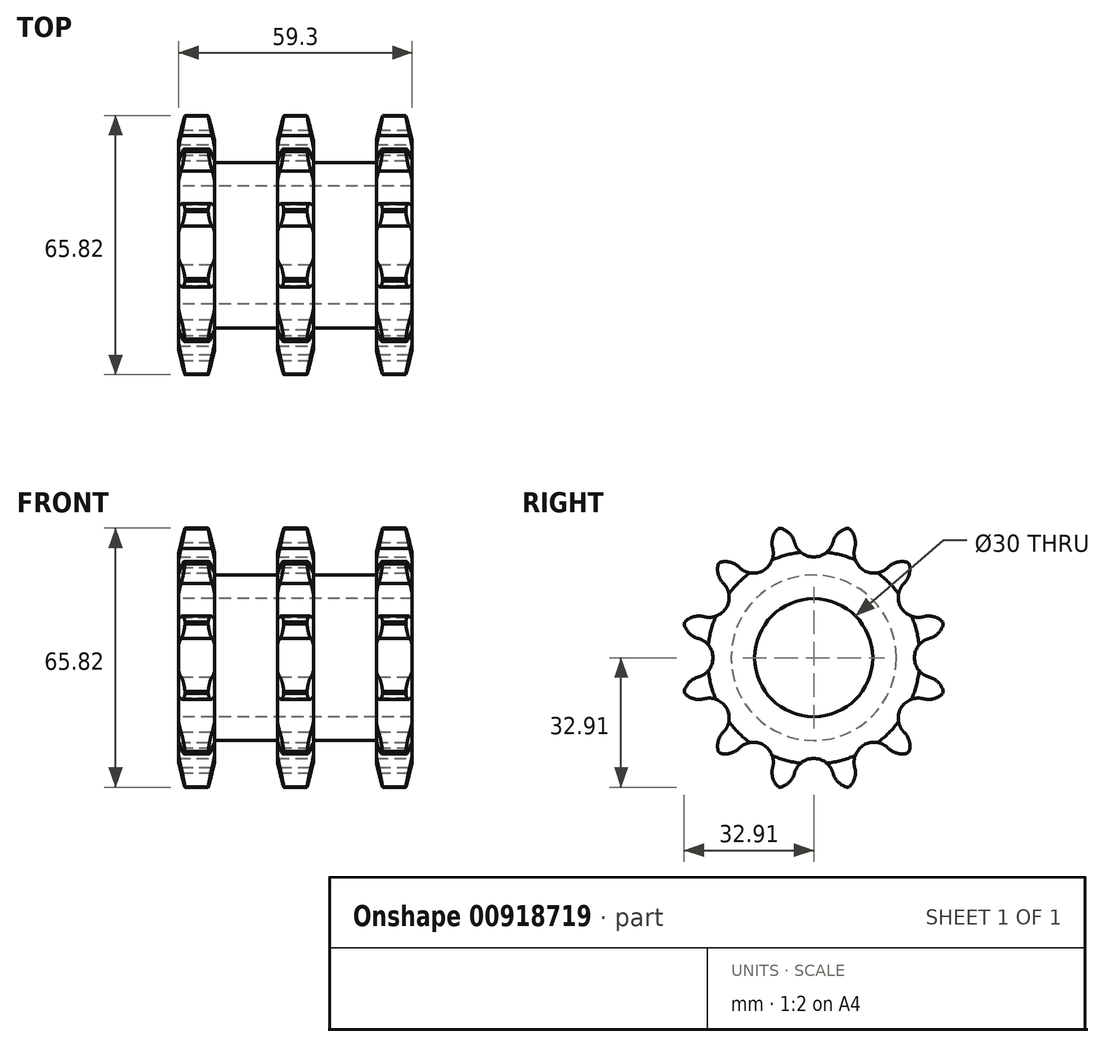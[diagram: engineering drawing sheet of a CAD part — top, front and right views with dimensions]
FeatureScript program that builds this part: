
annotation { "Feature Type Name" : "Feature", "Feature Type Description" : "" }
export const myFeature = defineFeature(function(context is Context, id is Id, definition is map)
    precondition{}
    {
        {
            var Q0;
            Q0=qCreatedBy(makeId("Front.planeOp"),FACE);
            var sketch = newSketch(context, id + "F0", { "sketchPlane" : qUnion([Q0])});
            skLineSegment(sketch, "E0", {"start": v(-60.79, 0) * mm, "end": v(61.07, 0) * mm, "construction": true});
            skLineSegment(sketch, "E1.bottom", {"start": v(-59.3, 34) * mm, "end": v(-50.2, 34) * mm});
            skLineSegment(sketch, "E1.top", {"start": v(-59.3, 15) * mm, "end": v(0, 15) * mm});
            skLineSegment(sketch, "E1.left", {"start": v(-59.3, 34) * mm, "end": v(-59.3, 15) * mm});
            skLineSegment(sketch, "E1.right", {"start": v(-50.2, 34) * mm, "end": v(-50.2, 21) * mm});
            skLineSegment(sketch, "E2.bottom", {"start": v(-50.2, 21) * mm, "end": v(-34.2, 21) * mm});
            skLineSegment(sketch, "E2.top", {"start": v(-59.3, 15) * mm, "end": v(-34.2, 15) * mm});
            skLineSegment(sketch, "E2.left", {"start": v(-59.3, 21) * mm, "end": v(-59.3, 15) * mm});
            skLineSegment(sketch, "E3.bottom", {"start": v(-34.2, 34) * mm, "end": v(-25.1, 34) * mm});
            skLineSegment(sketch, "E3.top", {"start": v(-34.2, 15) * mm, "end": v(-25.1, 15) * mm});
            skLineSegment(sketch, "E3.left", {"start": v(-34.2, 34) * mm, "end": v(-34.2, 21) * mm});
            skLineSegment(sketch, "E3.right", {"start": v(-25.1, 34) * mm, "end": v(-25.1, 21) * mm});
            skLineSegment(sketch, "E4.bottom", {"start": v(-25.1, 21) * mm, "end": v(-9.1, 21) * mm});
            skLineSegment(sketch, "E4.top", {"start": v(0, 15) * mm, "end": v(0, 15) * mm});
            skLineSegment(sketch, "E5", {"start": v(0, 15) * mm, "end": v(0, -11) * mm, "construction": true});
            skLineSegment(sketch, "E6.bottom", {"start": v(-9.1, 15) * mm, "end": v(0, 15) * mm});
            skLineSegment(sketch, "E6.top", {"start": v(-9.1, 34) * mm, "end": v(0, 34) * mm});
            skLineSegment(sketch, "E6.left", {"start": v(0, 15) * mm, "end": v(0, 34) * mm});
            skLineSegment(sketch, "E6.right", {"start": v(-9.1, 21) * mm, "end": v(-9.1, 34) * mm});
            skPoint(sketch, "E7.orphan", {"position": v(-50.2, 15) * mm});
            skPoint(sketch, "E8.orphan", {"position": v(0, 43.23) * mm});
            skSolve(sketch);
        }
        {
            var Q0;
            Q0=makeQuery(id+"F0.imprint","IMPRINT",FACE,{"disambiguationData":[TD([[makeQuery(id+"F0.imprint","IMPRINT",EDGE,{"derivedFrom":sQuery(id+"F0.wireOp",EDGE,"E1.bottom")}),-1.0]])]});
            var Q1;
            Q1=sQuery(id+"F0.wireOp",EDGE,"E0");
            revolve(context, id + "F1", {"surfaceOperationType" : NewSurfaceOperationType.NEW, "entities" : qUnion([Q0]), "axis" : qUnion([Q1]), "revolveType" : RevolveType.FULL});
        }
        {
            var Q0;
            Q0=makeQuery(id+"F1.opRevolve","SWEPT_FACE",FACE,{"disambiguationData":[OSD([sQuery(id+"F0.wireOp",EDGE,"E6.left")])]});
            var sketch = newSketch(context, id + "F2", { "sketchPlane" : qUnion([Q0])});
            skArc(sketch, "E9", {"start": v(-23.84, 24.24) * mm, "mid": v(-24.04, 24.04) * mm, "end": v(-24.24, 23.84) * mm});
            skCircle(sketch, "E10", {"center": v(0, 0) * mm, "radius": 30.67 * mm, "construction": true});
            skCircle(sketch, "E11", {"center": v(0, 0) * mm, "radius": 29.7 * mm, "construction": true});
            skLineSegment(sketch, "E12", {"start": v(0, 0) * mm, "end": v(5.78, 30.12) * mm, "construction": true});
            skLineSegment(sketch, "E13", {"start": v(0, 0) * mm, "end": v(10.05, 28.98) * mm, "construction": true});
            skArc(sketch, "E14", {"start": v(8.53, 32.92) * mm, "mid": v(6.21, 31.61) * mm, "end": v(4.9, 29.3) * mm});
            skArc(sketch, "E15.1.0", {"start": v(-9.07, 32.77) * mm, "mid": v(-10.42, 30.48) * mm, "end": v(-10.41, 27.82) * mm});
            skArc(sketch, "E16.trimOffspring", {"start": v(10.41, 27.82) * mm, "mid": v(10.42, 30.48) * mm, "end": v(9.07, 32.77) * mm});
            skArc(sketch, "E17.trimOffspring", {"start": v(-4.9, 29.36) * mm, "mid": v(-0.03, 25.6) * mm, "end": v(4.9, 29.3) * mm});
            skArc(sketch, "E18.trimOffspring", {"start": v(-4.9, 29.3) * mm, "mid": v(-6.21, 31.61) * mm, "end": v(-8.53, 32.92) * mm});
            skArc(sketch, "E19.1.0", {"start": v(-18.93, 22.97) * mm, "mid": v(-12.82, 22.15) * mm, "end": v(-10.41, 27.82) * mm});
            skArc(sketch, "E19.2.0", {"start": v(-27.88, 10.43) * mm, "mid": v(-22.18, 12.77) * mm, "end": v(-22.93, 18.89) * mm});
            skArc(sketch, "E19.3.0", {"start": v(-29.36, -4.9) * mm, "mid": v(-25.6, -0.03) * mm, "end": v(-29.3, 4.9) * mm});
            skArc(sketch, "E19.4.0", {"start": v(-22.97, -18.92) * mm, "mid": v(-22.15, -12.82) * mm, "end": v(-27.82, -10.4) * mm});
            skArc(sketch, "E19.5.0", {"start": v(-10.43, -27.87) * mm, "mid": v(-12.77, -22.17) * mm, "end": v(-18.88, -22.92) * mm});
            skArc(sketch, "E19.6.0", {"start": v(4.9, -29.35) * mm, "mid": v(0.03, -25.59) * mm, "end": v(-4.9, -29.3) * mm});
            skArc(sketch, "E19.7.0", {"start": v(18.93, -22.97) * mm, "mid": v(12.82, -22.14) * mm, "end": v(10.41, -27.81) * mm});
            skArc(sketch, "E19.8.0", {"start": v(27.88, -10.42) * mm, "mid": v(22.18, -12.77) * mm, "end": v(22.93, -18.88) * mm});
            skArc(sketch, "E19.9.0", {"start": v(29.36, 4.91) * mm, "mid": v(25.6, 0.03) * mm, "end": v(29.3, -4.89) * mm});
            skArc(sketch, "E19.10.0", {"start": v(22.97, 18.93) * mm, "mid": v(22.15, 12.82) * mm, "end": v(27.82, 10.42) * mm});
            skArc(sketch, "E19.11.0", {"start": v(10.43, 27.88) * mm, "mid": v(12.77, 22.18) * mm, "end": v(18.88, 22.93) * mm});
            skArc(sketch, "E20.1.0", {"start": v(-9.07, 32.77) * mm, "mid": v(-10.43, 30.48) * mm, "end": v(-10.41, 27.82) * mm});
            skArc(sketch, "E20.2.0", {"start": v(-24.24, 23.84) * mm, "mid": v(-24.27, 21.18) * mm, "end": v(-22.93, 18.89) * mm});
            skArc(sketch, "E20.3.0", {"start": v(-32.91, 8.53) * mm, "mid": v(-31.6, 6.21) * mm, "end": v(-29.3, 4.9) * mm});
            skArc(sketch, "E20.4.0", {"start": v(-32.77, -9.07) * mm, "mid": v(-30.48, -10.42) * mm, "end": v(-27.82, -10.4) * mm});
            skArc(sketch, "E20.5.0", {"start": v(-23.84, -24.24) * mm, "mid": v(-21.18, -24.26) * mm, "end": v(-18.88, -22.92) * mm});
            skArc(sketch, "E20.6.0", {"start": v(-8.53, -32.9) * mm, "mid": v(-6.21, -31.6) * mm, "end": v(-4.9, -29.3) * mm});
            skArc(sketch, "E20.7.0", {"start": v(9.07, -32.76) * mm, "mid": v(10.43, -30.47) * mm, "end": v(10.41, -27.81) * mm});
            skArc(sketch, "E20.8.0", {"start": v(24.24, -23.84) * mm, "mid": v(24.27, -21.18) * mm, "end": v(22.93, -18.88) * mm});
            skArc(sketch, "E20.9.0", {"start": v(32.91, -8.52) * mm, "mid": v(31.6, -6.2) * mm, "end": v(29.3, -4.89) * mm});
            skArc(sketch, "E20.10.0", {"start": v(32.77, 9.07) * mm, "mid": v(30.48, 10.43) * mm, "end": v(27.82, 10.42) * mm});
            skArc(sketch, "E20.11.0", {"start": v(23.84, 24.24) * mm, "mid": v(21.18, 24.27) * mm, "end": v(18.88, 22.93) * mm});
            skArc(sketch, "E21.2.0", {"start": v(-18.88, 22.93) * mm, "mid": v(-21.18, 24.27) * mm, "end": v(-23.84, 24.24) * mm});
            skArc(sketch, "E21.3.0", {"start": v(-27.82, 10.42) * mm, "mid": v(-30.48, 10.43) * mm, "end": v(-32.77, 9.07) * mm});
            skArc(sketch, "E21.4.0", {"start": v(-29.3, -4.89) * mm, "mid": v(-31.6, -6.2) * mm, "end": v(-32.91, -8.52) * mm});
            skArc(sketch, "E21.5.0", {"start": v(-22.93, -18.88) * mm, "mid": v(-24.27, -21.18) * mm, "end": v(-24.24, -23.84) * mm});
            skArc(sketch, "E21.6.0", {"start": v(-10.41, -27.81) * mm, "mid": v(-10.42, -30.47) * mm, "end": v(-9.07, -32.76) * mm});
            skArc(sketch, "E21.7.0", {"start": v(4.9, -29.3) * mm, "mid": v(6.21, -31.6) * mm, "end": v(8.53, -32.9) * mm});
            skArc(sketch, "E21.8.0", {"start": v(18.88, -22.92) * mm, "mid": v(21.18, -24.26) * mm, "end": v(23.84, -24.24) * mm});
            skArc(sketch, "E21.9.0", {"start": v(27.82, -10.4) * mm, "mid": v(30.48, -10.42) * mm, "end": v(32.77, -9.07) * mm});
            skArc(sketch, "E21.10.0", {"start": v(29.3, 4.9) * mm, "mid": v(31.6, 6.21) * mm, "end": v(32.91, 8.53) * mm});
            skArc(sketch, "E21.11.0", {"start": v(22.93, 18.89) * mm, "mid": v(24.27, 21.19) * mm, "end": v(24.24, 23.85) * mm});
            skArc(sketch, "E22.trimOffspring", {"start": v(-32.77, 9.07) * mm, "mid": v(-32.84, 8.8) * mm, "end": v(-32.91, 8.53) * mm});
            skArc(sketch, "E23.trimOffspring", {"start": v(-32.91, -8.52) * mm, "mid": v(-32.84, -8.8) * mm, "end": v(-32.77, -9.07) * mm});
            skArc(sketch, "E24.trimOffspring", {"start": v(-24.24, -23.84) * mm, "mid": v(-24.04, -24.04) * mm, "end": v(-23.84, -24.24) * mm});
            skArc(sketch, "E25.trimOffspring", {"start": v(-9.07, -32.76) * mm, "mid": v(-8.8, -32.84) * mm, "end": v(-8.53, -32.9) * mm});
            skArc(sketch, "E26.trimOffspring", {"start": v(8.53, -32.9) * mm, "mid": v(8.8, -32.84) * mm, "end": v(9.07, -32.76) * mm});
            skArc(sketch, "E27.trimOffspring", {"start": v(23.84, -24.24) * mm, "mid": v(24.04, -24.04) * mm, "end": v(24.24, -23.84) * mm});
            skArc(sketch, "E28.trimOffspring", {"start": v(32.77, -9.07) * mm, "mid": v(32.84, -8.8) * mm, "end": v(32.91, -8.52) * mm});
            skArc(sketch, "E29.trimOffspring", {"start": v(32.91, 8.53) * mm, "mid": v(32.84, 8.8) * mm, "end": v(32.77, 9.07) * mm});
            skArc(sketch, "E30.trimOffspring", {"start": v(24.24, 23.85) * mm, "mid": v(24.04, 24.05) * mm, "end": v(23.84, 24.24) * mm});
            skArc(sketch, "E31.trimOffspring", {"start": v(9.07, 32.77) * mm, "mid": v(8.8, 32.84) * mm, "end": v(8.53, 32.92) * mm});
            skArc(sketch, "E32.trimOffspring", {"start": v(-8.53, 32.92) * mm, "mid": v(-8.8, 32.84) * mm, "end": v(-9.07, 32.77) * mm});
            skSolve(sketch);
        }
        {
            var Q0;
            Q0=makeQuery(id+"F1.opRevolve","SWEPT_EDGE",EDGE,{"disambiguationData":[OSD([sQuery(id+"F0.wireOp",EDGE,"E6.top"),sQuery(id+"F0.wireOp",EDGE,"E6.right")])]});
            var Q1;
            Q1=makeQuery(id+"F1.opRevolve","SWEPT_EDGE",EDGE,{"disambiguationData":[OSD([sQuery(id+"F0.wireOp",EDGE,"E3.bottom"),sQuery(id+"F0.wireOp",EDGE,"E3.left")])]});
            var Q2;
            Q2=makeQuery(id+"F1.opRevolve","SWEPT_EDGE",EDGE,{"disambiguationData":[OSD([sQuery(id+"F0.wireOp",EDGE,"E1.bottom"),sQuery(id+"F0.wireOp",EDGE,"E1.left")])]});
            chamfer(context, id + "F3", {"entities" : qUnion([Q0, Q1, Q2]), "chamferType" : ChamferType.TWO_OFFSETS, "width1" : 7 * mm, "oppositeDirection" : false, "width2" : 1.6 * mm, "tangentPropagation" : true});
        }
        {
            var Q0;
            Q0=makeQuery(id+"F1.opRevolve","SWEPT_EDGE",EDGE,{"disambiguationData":[OSD([sQuery(id+"F0.wireOp",EDGE,"E6.top"),sQuery(id+"F0.wireOp",EDGE,"E6.left")])]});
            var Q1;
            Q1=makeQuery(id+"F1.opRevolve","SWEPT_EDGE",EDGE,{"disambiguationData":[OSD([sQuery(id+"F0.wireOp",EDGE,"E3.bottom"),sQuery(id+"F0.wireOp",EDGE,"E3.right")])]});
            var Q2;
            Q2=makeQuery(id+"F1.opRevolve","SWEPT_EDGE",EDGE,{"disambiguationData":[OSD([sQuery(id+"F0.wireOp",EDGE,"E1.bottom"),sQuery(id+"F0.wireOp",EDGE,"E1.right")])]});
            chamfer(context, id + "F4", {"entities" : qUnion([Q0, Q1, Q2]), "chamferType" : ChamferType.TWO_OFFSETS, "width1" : 1.6 * mm, "oppositeDirection" : false, "width2" : 7 * mm, "tangentPropagation" : true});
        }
        {
            var Q0;
            {var subQ37=sQuery(id+"F2.wireOp",EDGE,"E17.trimOffspring");Q0=makeQuery(id+"F2.imprint","IMPRINT",FACE,{"disambiguationData":[TD([[makeQuery(id+"F2.imprint","IMPRINT",EDGE,{"derivedFrom":subQ37}),-1.0]])]});}
            extrude(context, id + "F5", {"entities" : qUnion([Q0]), "operationType" : NewBodyOperationType.INTERSECT, "endBound" : BoundingType.THROUGH_ALL, "oppositeDirection" : true, "depth" : 25 * mm, "offsetDistance" : 25 * mm});
        }
    });
